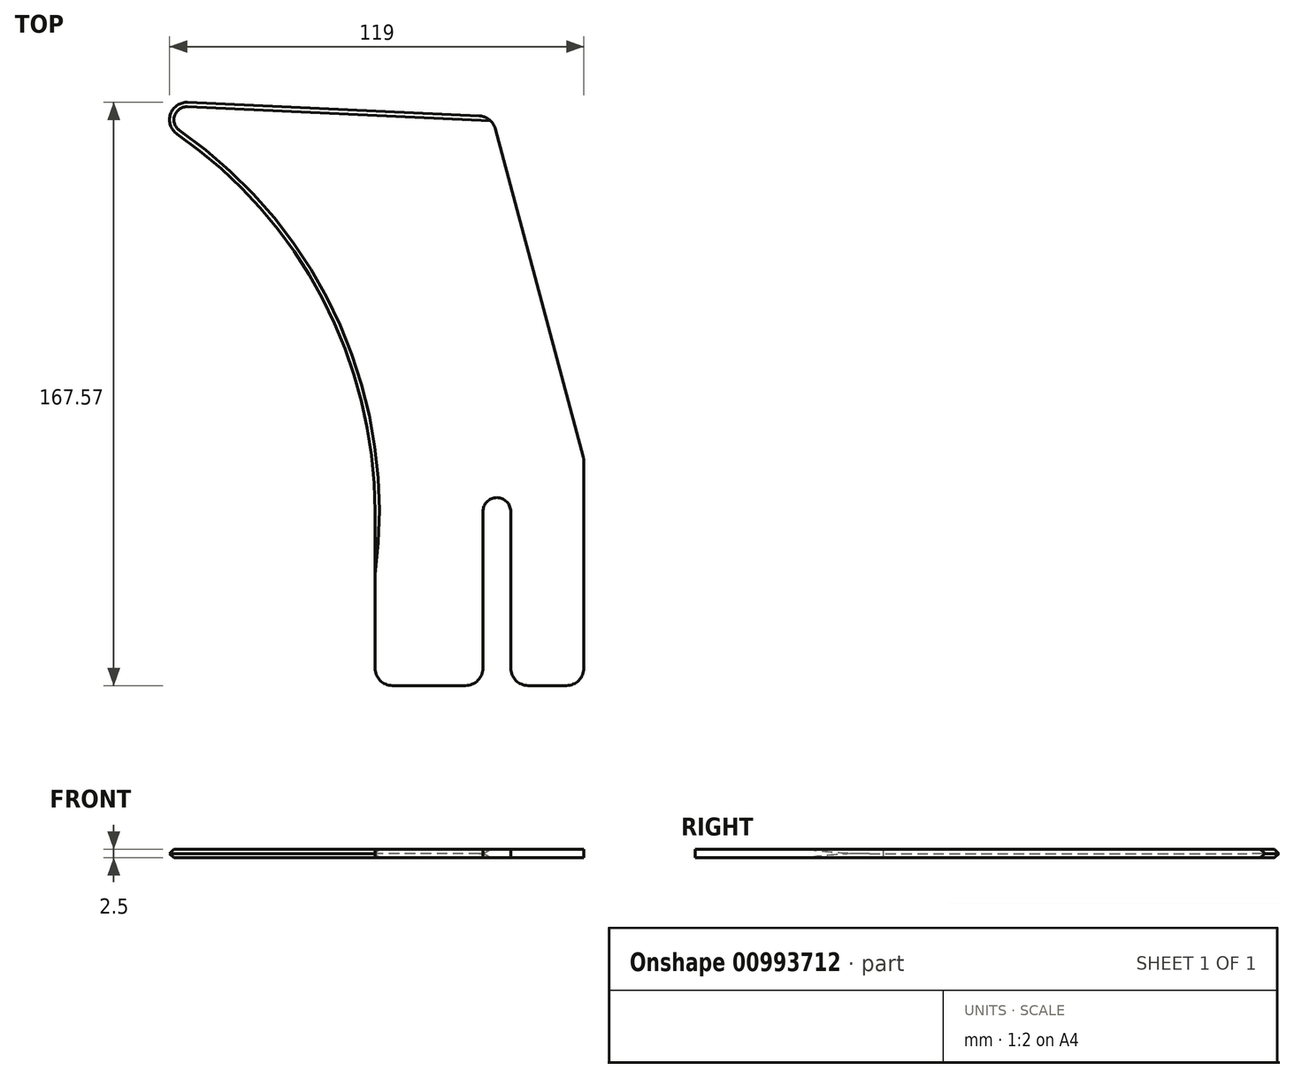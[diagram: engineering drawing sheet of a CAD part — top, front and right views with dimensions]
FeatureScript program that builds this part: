
annotation { "Feature Type Name" : "Feature", "Feature Type Description" : "" }
export const myFeature = defineFeature(function(context is Context, id is Id, definition is map)
    precondition{}
    {
        {
            var Q0;
            Q0=qCreatedBy(makeId("Top.planeOp"),FACE);
            var sketch = newSketch(context, id + "F0", { "sketchPlane" : qUnion([Q0])});
            skLineSegment(sketch, "E0", {"start": v(0, 0) * mm, "end": v(-21, 0) * mm});
            skLineSegment(sketch, "E1", {"start": v(-21, 0) * mm, "end": v(-21, 50) * mm});
            skLineSegment(sketch, "E2", {"start": v(-21, 50) * mm, "end": v(-29, 50) * mm, "construction": true});
            skLineSegment(sketch, "E3", {"start": v(-29, 50) * mm, "end": v(-29, 0) * mm});
            skLineSegment(sketch, "E4", {"start": v(-29, 0) * mm, "end": v(-60, 0) * mm});
            skLineSegment(sketch, "E5", {"start": v(-60, 0) * mm, "end": v(-60, 50) * mm});
            skLineSegment(sketch, "E6", {"start": v(0, 0) * mm, "end": v(0, 65) * mm});
            skLineSegment(sketch, "E7", {"start": v(-26.4, 163.5) * mm, "end": v(0, 65) * mm});
            skPoint(sketch, "E8.visualSharp", {"position": v(-134, 168.5) * mm});
            skPoint(sketch, "E9.visualSharp", {"position": v(-60, 0) * mm});
            skPoint(sketch, "E10.visualSharp", {"position": v(0, 0) * mm});
            skArc(sketch, "E11", {"start": v(-21, 50) * mm, "mid": v(-25, 54) * mm, "end": v(-29, 50) * mm});
            skLineSegment(sketch, "E12", {"start": v(-134, 168.5) * mm, "end": v(-26.4, 163.5) * mm});
            skPoint(sketch, "E13.visualSharp", {"position": v(-26.4, 163.5) * mm});
            skArc(sketch, "E14", {"start": v(-60, 50) * mm, "mid": v(-80.02, 119.85) * mm, "end": v(-134, 168.5) * mm});
            skSolve(sketch);
        }
        {
            var Q0;
            Q0=makeQuery(id+"F0.imprint","IMPRINT",FACE,{"disambiguationData":[TD([[makeQuery(id+"F0.imprint","IMPRINT",EDGE,{"derivedFrom":sQuery(id+"F0.wireOp",EDGE,"E0")}),-1.0]])]});
            var Q1;
            {var subQ0=sQuery(id+"F0.wireOp",EDGE,"C4Dev7UV-BONe-jzlM-jVuK-0DQgIFs9LGOA");Q1=makeQuery(id+"F0.imprint","IMPRINT",FACE,{"disambiguationData":[TD([[makeQuery(id+"F0.imprint","IMPRINT",EDGE,{"derivedFrom":subQ0}),-1.0]])]});}
            var Q2;
            {var subQ0=sQuery(id+"F0.wireOp",EDGE,"9TcCCysc-FSD2-n4vG-R1Fy-J1hU90iTH3EE");Q2=makeQuery(id+"F0.imprint","IMPRINT",FACE,{"disambiguationData":[TD([[makeQuery(id+"F0.imprint","IMPRINT",EDGE,{"derivedFrom":subQ0}),1.0]])]});}
            extrude(context, id + "F1", {"entities" : qUnion([Q0, Q1, Q2]), "depth" : 2.5 * mm, "offsetDistance" : 25 * mm});
        }
        {
            var Q0;
            Q0=makeQuery(id+"F1.opExtrude","SWEPT_EDGE",EDGE,{"disambiguationData":[OSD([sQuery(id+"F0.wireOp",EDGE,"E12"),sQuery(id+"F0.wireOp",EDGE,"E14")])]});
            var Q1;
            Q1=makeQuery(id+"F1.opExtrude","SWEPT_EDGE",EDGE,{"disambiguationData":[OSD([sQuery(id+"F0.wireOp",EDGE,"E7"),sQuery(id+"F0.wireOp",EDGE,"E12")])]});
            var Q2;
            Q2=makeQuery(id+"F1.opExtrude","SWEPT_EDGE",EDGE,{"disambiguationData":[OSD([sQuery(id+"F0.wireOp",EDGE,"E6"),sQuery(id+"F0.wireOp",EDGE,"E7")])]});
            var Q3;
            Q3=makeQuery(id+"F1.opExtrude","SWEPT_EDGE",EDGE,{"disambiguationData":[OSD([sQuery(id+"F0.wireOp",EDGE,"E0"),sQuery(id+"F0.wireOp",EDGE,"E6")])]});
            var Q4;
            Q4=makeQuery(id+"F1.opExtrude","SWEPT_EDGE",EDGE,{"disambiguationData":[OSD([sQuery(id+"F0.wireOp",EDGE,"E3"),sQuery(id+"F0.wireOp",EDGE,"E4")])]});
            var Q5;
            Q5=makeQuery(id+"F1.opExtrude","SWEPT_EDGE",EDGE,{"disambiguationData":[OSD([sQuery(id+"F0.wireOp",EDGE,"E0"),sQuery(id+"F0.wireOp",EDGE,"E1")])]});
            var Q6;
            Q6=makeQuery(id+"F1.opExtrude","SWEPT_EDGE",EDGE,{"disambiguationData":[OSD([sQuery(id+"F0.wireOp",EDGE,"E4"),sQuery(id+"F0.wireOp",EDGE,"E5")])]});
            fillet(context, id + "F2", {"entities" : qUnion([Q0, Q1, Q2, Q3, Q4, Q5, Q6]), "radius" : 5 * mm, "tangentPropagation" : true, "allowEdgeOverflow" : false});
        }
        {
            var Q0;
            Q0=makeQuery(id+"F1.opExtrude","SWEPT_FACE",FACE,{"disambiguationData":[OSD([sQuery(id+"F0.wireOp",EDGE,"E14")])]});
            var Q1;
            Q1=makeQuery(id+"F2.opFillet","BLEND_FACE",FACE,{"disambiguationData":[OSD([sQuery(id+"F0.wireOp",EDGE,"E12"),sQuery(id+"F0.wireOp",EDGE,"E14")])]});
            var Q2;
            Q2=makeQuery(id+"F1.opExtrude","SWEPT_FACE",FACE,{"disambiguationData":[OSD([sQuery(id+"F0.wireOp",EDGE,"E12")])]});
            chamfer(context, id + "F3", {"entities" : qUnion([Q0, Q1, Q2]), "width" : (2.5 / 2) * mm});
        }
    });
